# Revit family: Shower-Shower_Column_Kit-KOHLER-COMPOSED-K-73111T_1
name_source: partatom
category: Plumbing Fixtures
revit_build: Autodesk Revit 2017 (Build: 20160225_1515(x64)
units: mm (PartAtom-declared; Revit-internal decimal feet)

## family parameters
Cut with Voids When Loaded = No
Host = Face
OmniClass Number = 23.31.17.00
OmniClass Title = Showers
Part Type = Normal
Room Calculation Point = No
Round Connector Dimension = Use Diameter
Shared = No

## types (11) — shared parameters
ADA Compliant = No
Assembly Code = D2010700
CW Connection = Yes
Cold Water Inlet = Cold Water Inlet
Date Modified = 12/02/2020
Default Elevation = 36"
Drain Included = No
Flow Rate = 2 GPM
HW Connection = Yes
Height = 47 1/4"
Hot Water Inlet = Hot Water Inlet
Length = 23 3/8"
Manufacturer = KOHLER Co.
Master Format 2014 = 22 42 23
Master Format 2014 Name = Residential Showers
Material = Premium Metal Construction
Pressure = 45.00 psi
Product Documentation Link = https://files.kohler.com.cn
Product Name = COMPOSED
Product Page URL = https://www.kohler.com.cn
Spout Reach = 8 5/16"
URL = https://www.kohler.com.cn
Vent Connection = No
Waste Connection = No
Waste Water Outlet = Waste Water Outlet
WaterSense Certified = No
Width = 13 13/16"

## per-type parameters (varying)
| type | Description | Finish | Handle Finish | Model | Round Handshower | Squre Handshower | Type |
| CP-Polished Chrome | Thermostatic three-outlet shower column hard pipe connection | Kohler-Metal-CP-Polished_Chrome | Kohler-Metal-CP-Polished_Chrome | K-73111T-7-CP | No | Yes | 1 |
| AF-Flange Gold | Thermostatic three-outlet shower column hard pipe connection | Kohler-Metal-AF-Flange_Gold | Kohler-Metal-AF-Flange_Gold | K-73111T-7-AF | No | Yes | 2 |
| BN-Roman Silver | Thermostatic three-outlet shower column hard pipe connection | Kohler-Metal-BN-Roman_Silver | Kohler-Metal-BN-Roman_Silver | K-73111T-7-BN | No | Yes | 3 |
| BV-Roman Copper | Thermostatic three-outlet shower column hard pipe connection | Kohler-Metal-BV-Roman_Copper | Kohler-Metal-BV-Roman_Copper | K-73111T-7-BV | No | Yes | 4 |
| SN-Champagne Gold | Thermostatic three-outlet shower column hard pipe connection | Kohler-Metal-SN-Champagne_Gold | Kohler-Metal-SN-Champagne_Gold | K-73111T-7-SN | No | Yes | 5 |
| PGD-Eternal Gold | Thermostatic three-outlet shower column hard pipe connection | Kohler-Metal-PGD-Eternal_Gold | Kohler-Metal-PGD-Eternal_Gold | K-73111T-7-PGD | No | Yes | 6 |
| RGD-Rose Gold | Thermostatic three-outlet shower column hard pipe connection | Kohler-Metal-RGD-Rose_Gold | Kohler-Metal-RGD-Rose_Gold | K-73111T-7-RGD | No | Yes | 7 |
| TT-Titanium Silver | Thermostatic three-outlet shower column hard pipe connection | Kohler-Metal-TT-Titanium_Silver | Kohler-Metal-TT-Titanium_Silver | K-73111T-7-TT | No | Yes | 8 |
| 2BL-Original Black | Thermostatic three-outlet shower column hard pipe connection | Kohler-Metal-2BL-Original_Black | Kohler-Metal-2BL-Original_Black | K-73111T-7-2BL | No | Yes | 9 |
| Manchester United limited Edition, BL-Original Black | Thermostatic three-outlet shower column hard pipe connection (Manchester United limited edition) | Kohler-Metal-BL-Matte_Black | Kohler-Metal-BL-Matte_Black | K-73111T-7MU-BL | Yes | No | 10 |
| Manchester United limited Edition, BLR-Primary Black Red | Thermostatic three-outlet shower column hard pipe connection (Manchester United limited edition) | Kohler-Metal-BL-Matte_Black | Kohler-Metal-Red | K-73111T-7MU-BLR | Yes | No | 11 |

## geometry (parser evidence)
native form markers: Sweep x5
no freeform markers — native parametric forms only
